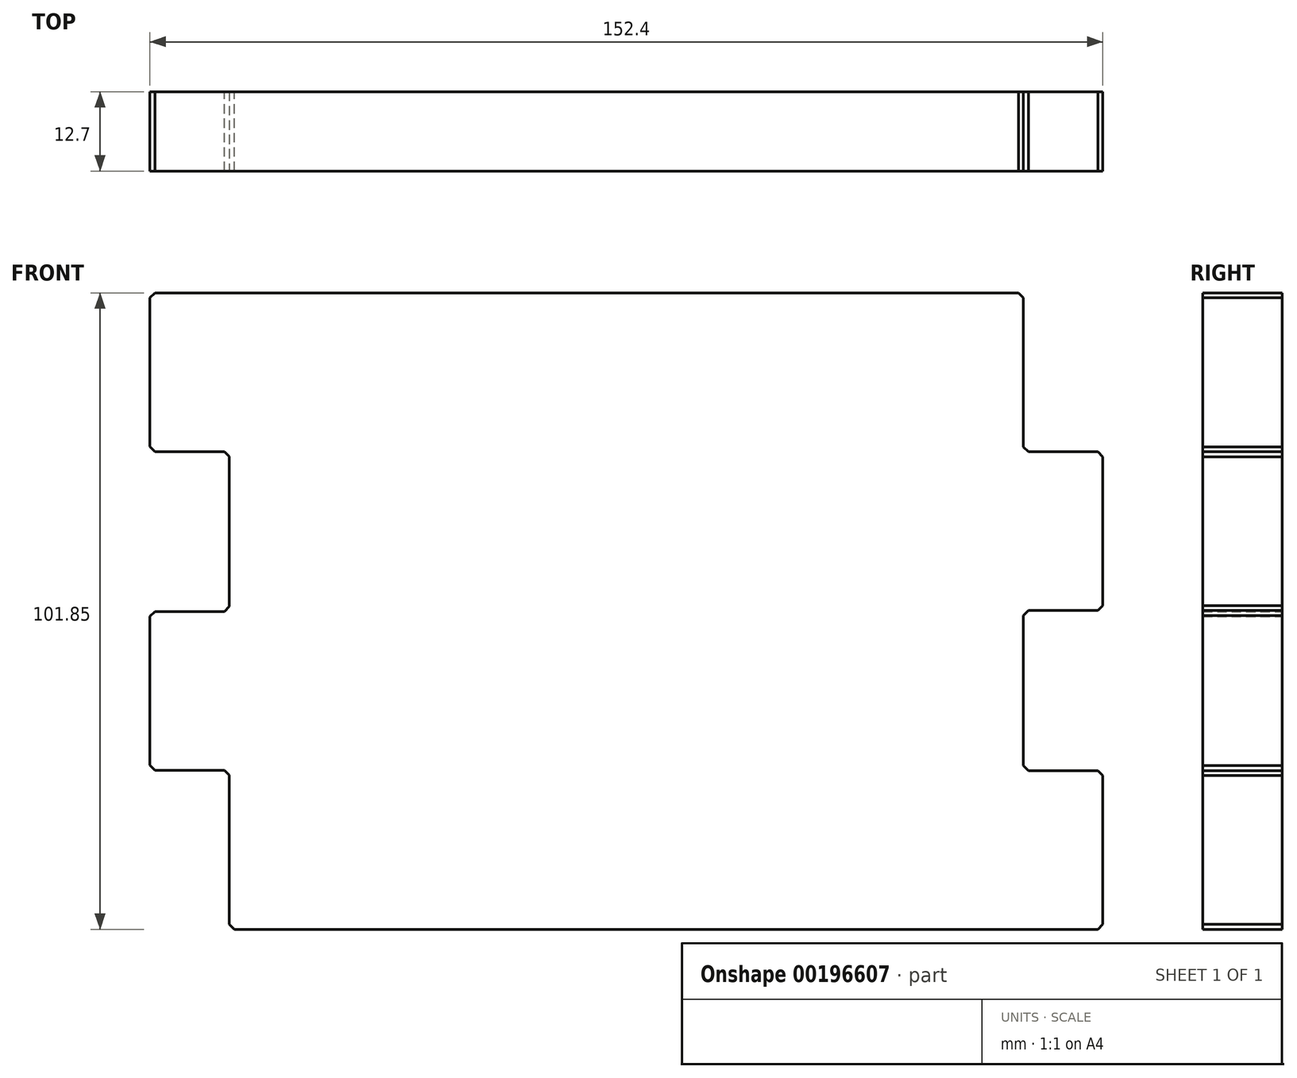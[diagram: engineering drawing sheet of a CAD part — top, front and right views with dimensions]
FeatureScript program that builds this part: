
annotation { "Feature Type Name" : "Feature", "Feature Type Description" : "" }
export const myFeature = defineFeature(function(context is Context, id is Id, definition is map)
    precondition{}
    {
        {
            var Q0;
            Q0=qCreatedBy(makeId("Front.planeOp"),FACE);
            var sketch = newSketch(context, id + "F0", { "sketchPlane" : qUnion([Q0])});
            skLineSegment(sketch, "E0.bottom", {"start": v(-63.5, 0) * mm, "end": v(76.2, 0) * mm});
            skLineSegment(sketch, "E0.top", {"start": v(-76.2, 101.85) * mm, "end": v(63.5, 101.85) * mm});
            skLineSegment(sketch, "E0.left", {"start": v(-76.2, 0) * mm, "end": v(-76.2, 101.85) * mm, "construction": true});
            skLineSegment(sketch, "E0.right", {"start": v(76.2, 0) * mm, "end": v(76.2, 101.85) * mm, "construction": true});
            skLineSegment(sketch, "E1", {"start": v(0, 0) * mm, "end": v(0, 101.85) * mm, "construction": true});
            skLineSegment(sketch, "E2", {"start": v(-76.2, 76.45) * mm, "end": v(-63.5, 76.45) * mm});
            skLineSegment(sketch, "E3", {"start": v(-63.5, 50.85) * mm, "end": v(-76.2, 50.85) * mm});
            skLineSegment(sketch, "E4", {"start": v(-76.2, 25.45) * mm, "end": v(-63.5, 25.45) * mm});
            skLineSegment(sketch, "E5", {"start": v(-76.2, 0) * mm, "end": v(-63.5, 0) * mm, "construction": true});
            skLineSegment(sketch, "E6", {"start": v(63.5, 101.85) * mm, "end": v(76.2, 101.85) * mm, "construction": true});
            skLineSegment(sketch, "E7", {"start": v(-76.2, 101.85) * mm, "end": v(-76.2, 76.45) * mm});
            skLineSegment(sketch, "E8", {"start": v(-63.5, 76.45) * mm, "end": v(-63.5, 50.85) * mm});
            skLineSegment(sketch, "E9", {"start": v(-76.2, 50.85) * mm, "end": v(-76.2, 25.45) * mm});
            skLineSegment(sketch, "E10", {"start": v(-63.5, 0) * mm, "end": v(-63.5, 25.45) * mm});
            skLineSegment(sketch, "E11", {"start": v(63.5, 101.85) * mm, "end": v(63.5, 76.4) * mm});
            skLineSegment(sketch, "E12", {"start": v(63.5, 76.4) * mm, "end": v(76.2, 76.4) * mm});
            skLineSegment(sketch, "E13", {"start": v(76.2, 76.4) * mm, "end": v(76.2, 51) * mm});
            skLineSegment(sketch, "E14", {"start": v(76.2, 51) * mm, "end": v(63.5, 51) * mm});
            skLineSegment(sketch, "E15", {"start": v(63.5, 51) * mm, "end": v(63.5, 25.4) * mm});
            skLineSegment(sketch, "E16", {"start": v(63.5, 25.4) * mm, "end": v(76.2, 25.4) * mm});
            skLineSegment(sketch, "E17", {"start": v(76.2, 25.4) * mm, "end": v(76.2, 0) * mm});
            skSolve(sketch);
        }
        {
            var Q0;
            Q0=makeQuery(id+"F0.imprint","IMPRINT",FACE,{"disambiguationData":[TD([[makeQuery(id+"F0.imprint","IMPRINT",EDGE,{"derivedFrom":sQuery(id+"F0.wireOp",EDGE,"E0.bottom")}),1.0]])]});
            extrude(context, id + "F1", {"entities" : qUnion([Q0]), "depth" : 12.7 * mm});
        }
        {
            var Q0;
            Q0=makeQuery(id+"F1.opExtrude","SWEPT_EDGE",EDGE,{"disambiguationData":[OSD([sQuery(id+"F0.wireOp",EDGE,"ySx5GVgK-PwMO-QeTF-d33c-qZHpJscomG8l"),sQuery(id+"F0.wireOp",EDGE,"E2")])]});
            var Q1;
            Q1=makeQuery(id+"F1.opExtrude","SWEPT_EDGE",EDGE,{"disambiguationData":[OSD([sQuery(id+"F0.wireOp",EDGE,"E2"),sQuery(id+"F0.wireOp",EDGE,"iYF5XFN9-ezYN-fZ6a-XmcD-MfN94p8ViovJ")])]});
            var Q2;
            Q2=makeQuery(id+"F1.opExtrude","SWEPT_EDGE",EDGE,{"disambiguationData":[OSD([sQuery(id+"F0.wireOp",EDGE,"iYF5XFN9-ezYN-fZ6a-XmcD-MfN94p8ViovJ"),sQuery(id+"F0.wireOp",EDGE,"E3")])]});
            var Q3;
            Q3=makeQuery(id+"F1.opExtrude","SWEPT_EDGE",EDGE,{"disambiguationData":[OSD([sQuery(id+"F0.wireOp",EDGE,"E3"),sQuery(id+"F0.wireOp",EDGE,"fn0HFarr-Vm6l-Wv9n-QxR3-8WWVWt37jal4")])]});
            var Q4;
            Q4=makeQuery(id+"F1.opExtrude","SWEPT_EDGE",EDGE,{"disambiguationData":[OSD([sQuery(id+"F0.wireOp",EDGE,"fn0HFarr-Vm6l-Wv9n-QxR3-8WWVWt37jal4"),sQuery(id+"F0.wireOp",EDGE,"E4")])]});
            var Q5;
            Q5=makeQuery(id+"F1.opExtrude","SWEPT_EDGE",EDGE,{"disambiguationData":[OSD([sQuery(id+"F0.wireOp",EDGE,"E4"),sQuery(id+"F0.wireOp",EDGE,"cv2dCayA-6eFW-g7PB-GLee-ynXXgVT8iGWb")])]});
            var Q6;
            Q6=makeQuery(id+"F1.opExtrude","SWEPT_EDGE",EDGE,{"disambiguationData":[OSD([sQuery(id+"F0.wireOp",EDGE,"E0.bottom"),sQuery(id+"F0.wireOp",EDGE,"cv2dCayA-6eFW-g7PB-GLee-ynXXgVT8iGWb")])]});
            var Q7;
            Q7=makeQuery(id+"F1.opExtrude","SWEPT_EDGE",EDGE,{"disambiguationData":[OSD([sQuery(id+"F0.wireOp",EDGE,"E0.top"),sQuery(id+"F0.wireOp",EDGE,"ySx5GVgK-PwMO-QeTF-d33c-qZHpJscomG8l")])]});
            var Q8;
            Q8=makeQuery(id+"F1.opExtrude","SWEPT_EDGE",EDGE,{"disambiguationData":[OSD([sQuery(id+"F0.wireOp",EDGE,"Hyyo0jbT-JM2b-UWpm-2w3v-t7ESnS4u2sGn"),sQuery(id+"F0.wireOp",EDGE,"pMrQEk6n-VmEf-EYRk-C8bL-S6TDwgkfhyU5")])]});
            var Q9;
            Q9=makeQuery(id+"F1.opExtrude","SWEPT_EDGE",EDGE,{"disambiguationData":[OSD([sQuery(id+"F0.wireOp",EDGE,"Vv8ZQEiE-BRnW-E4rS-U8ro-dSD8coYp8QJY"),sQuery(id+"F0.wireOp",EDGE,"Hyyo0jbT-JM2b-UWpm-2w3v-t7ESnS4u2sGn")])]});
            var Q10;
            Q10=makeQuery(id+"F1.opExtrude","SWEPT_EDGE",EDGE,{"disambiguationData":[OSD([sQuery(id+"F0.wireOp",EDGE,"E0.top"),sQuery(id+"F0.wireOp",EDGE,"pMrQEk6n-VmEf-EYRk-C8bL-S6TDwgkfhyU5")])]});
            var Q11;
            Q11=makeQuery(id+"F1.opExtrude","SWEPT_EDGE",EDGE,{"disambiguationData":[OSD([sQuery(id+"F0.wireOp",EDGE,"ZdUXTIXG-SnpK-IuKx-slpV-eRTzhFTIA9Kf"),sQuery(id+"F0.wireOp",EDGE,"Vv8ZQEiE-BRnW-E4rS-U8ro-dSD8coYp8QJY")])]});
            var Q12;
            Q12=makeQuery(id+"F1.opExtrude","SWEPT_EDGE",EDGE,{"disambiguationData":[OSD([sQuery(id+"F0.wireOp",EDGE,"StArgF25-okTD-DuiF-PlWP-4kf2dGjtNRSu"),sQuery(id+"F0.wireOp",EDGE,"kJGFMyQB-xWel-AxLR-raAn-4D2uW22Zhopa")])]});
            var Q13;
            Q13=makeQuery(id+"F1.opExtrude","SWEPT_EDGE",EDGE,{"disambiguationData":[OSD([sQuery(id+"F0.wireOp",EDGE,"gMyCbveq-12uZ-DG1z-p0m1-6uREQ3wlWfBy"),sQuery(id+"F0.wireOp",EDGE,"StArgF25-okTD-DuiF-PlWP-4kf2dGjtNRSu")])]});
            var Q14;
            Q14=makeQuery(id+"F1.opExtrude","SWEPT_EDGE",EDGE,{"disambiguationData":[OSD([sQuery(id+"F0.wireOp",EDGE,"E0.bottom"),sQuery(id+"F0.wireOp",EDGE,"gMyCbveq-12uZ-DG1z-p0m1-6uREQ3wlWfBy")])]});
            var Q15;
            Q15=makeQuery(id+"F1.opExtrude","SWEPT_EDGE",EDGE,{"disambiguationData":[OSD([sQuery(id+"F0.wireOp",EDGE,"kJGFMyQB-xWel-AxLR-raAn-4D2uW22Zhopa"),sQuery(id+"F0.wireOp",EDGE,"ZdUXTIXG-SnpK-IuKx-slpV-eRTzhFTIA9Kf")])]});
            var Q16;
            Q16=makeQuery(id+"F1.opExtrude","SWEPT_EDGE",EDGE,{"disambiguationData":[OSD([sQuery(id+"F0.wireOp",EDGE,"E12"),sQuery(id+"F0.wireOp",EDGE,"E13")])]});
            var Q17;
            Q17=makeQuery(id+"F1.opExtrude","SWEPT_EDGE",EDGE,{"disambiguationData":[OSD([sQuery(id+"F0.wireOp",EDGE,"E11"),sQuery(id+"F0.wireOp",EDGE,"E12")])]});
            var Q18;
            Q18=makeQuery(id+"F1.opExtrude","SWEPT_EDGE",EDGE,{"disambiguationData":[OSD([sQuery(id+"F0.wireOp",EDGE,"E15"),sQuery(id+"F0.wireOp",EDGE,"E16")])]});
            var Q19;
            Q19=makeQuery(id+"F1.opExtrude","SWEPT_EDGE",EDGE,{"disambiguationData":[OSD([sQuery(id+"F0.wireOp",EDGE,"E16"),sQuery(id+"F0.wireOp",EDGE,"E17")])]});
            var Q20;
            Q20=makeQuery(id+"F1.opExtrude","SWEPT_EDGE",EDGE,{"disambiguationData":[OSD([sQuery(id+"F0.wireOp",EDGE,"E13"),sQuery(id+"F0.wireOp",EDGE,"E14")])]});
            var Q21;
            Q21=makeQuery(id+"F1.opExtrude","SWEPT_EDGE",EDGE,{"disambiguationData":[OSD([sQuery(id+"F0.wireOp",EDGE,"E14"),sQuery(id+"F0.wireOp",EDGE,"E15")])]});
            chamfer(context, id + "F2", {"entities" : qUnion([Q0, Q1, Q2, Q3, Q4, Q5, Q6, Q7, Q8, Q9, Q10, Q11, Q12, Q13, Q14, Q15, Q16, Q17, Q18, Q19, Q20, Q21]), "width" : 0.8 * mm, "tangentPropagation" : true});
        }
    });
